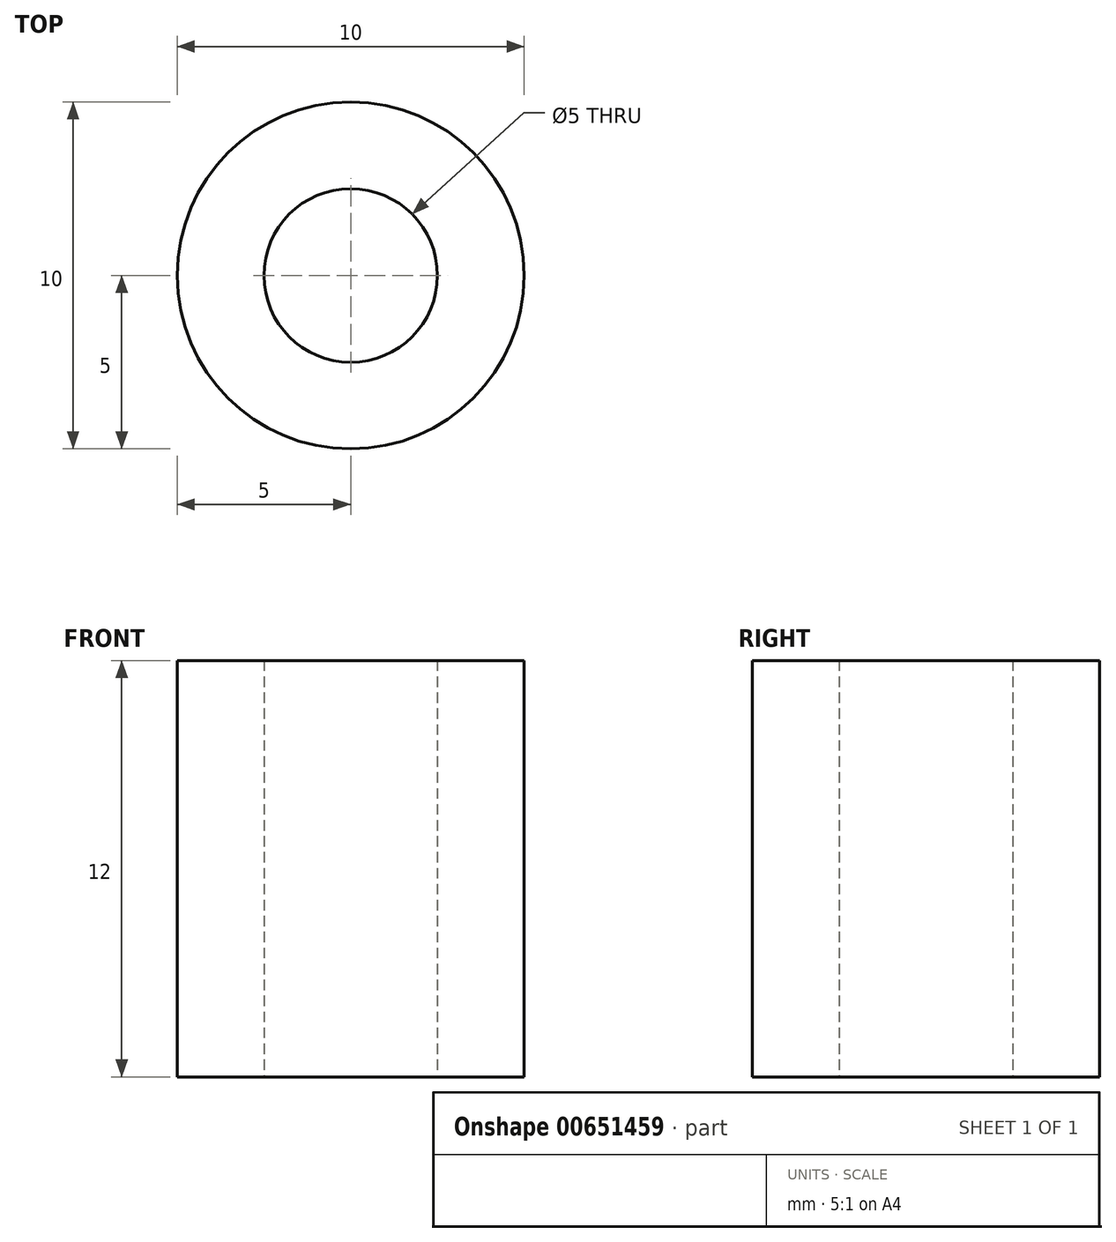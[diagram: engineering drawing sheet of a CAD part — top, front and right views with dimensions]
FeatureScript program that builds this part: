
annotation { "Feature Type Name" : "Feature", "Feature Type Description" : "" }
export const myFeature = defineFeature(function(context is Context, id is Id, definition is map)
    precondition{}
    {
        {
            var Q0;
            Q0=qCreatedBy(makeId("Top.planeOp"),FACE);
            var sketch = newSketch(context, id + "F0", { "sketchPlane" : qUnion([Q0])});
            skCircle(sketch, "E0", {"center": v(0, 0) * mm, "radius": 2.5 * mm});
            skCircle(sketch, "E1", {"center": v(0, 0) * mm, "radius": 5 * mm});
            skSolve(sketch);
        }
        {
            var Q0;
            Q0 = qSketchRegion(id + "F0", true);
            extrude(context, id + "F1", {"entities" : qUnion([Q0]), "depth" : 12 * mm, "offsetDistance" : 25 * mm});
        }
    });
